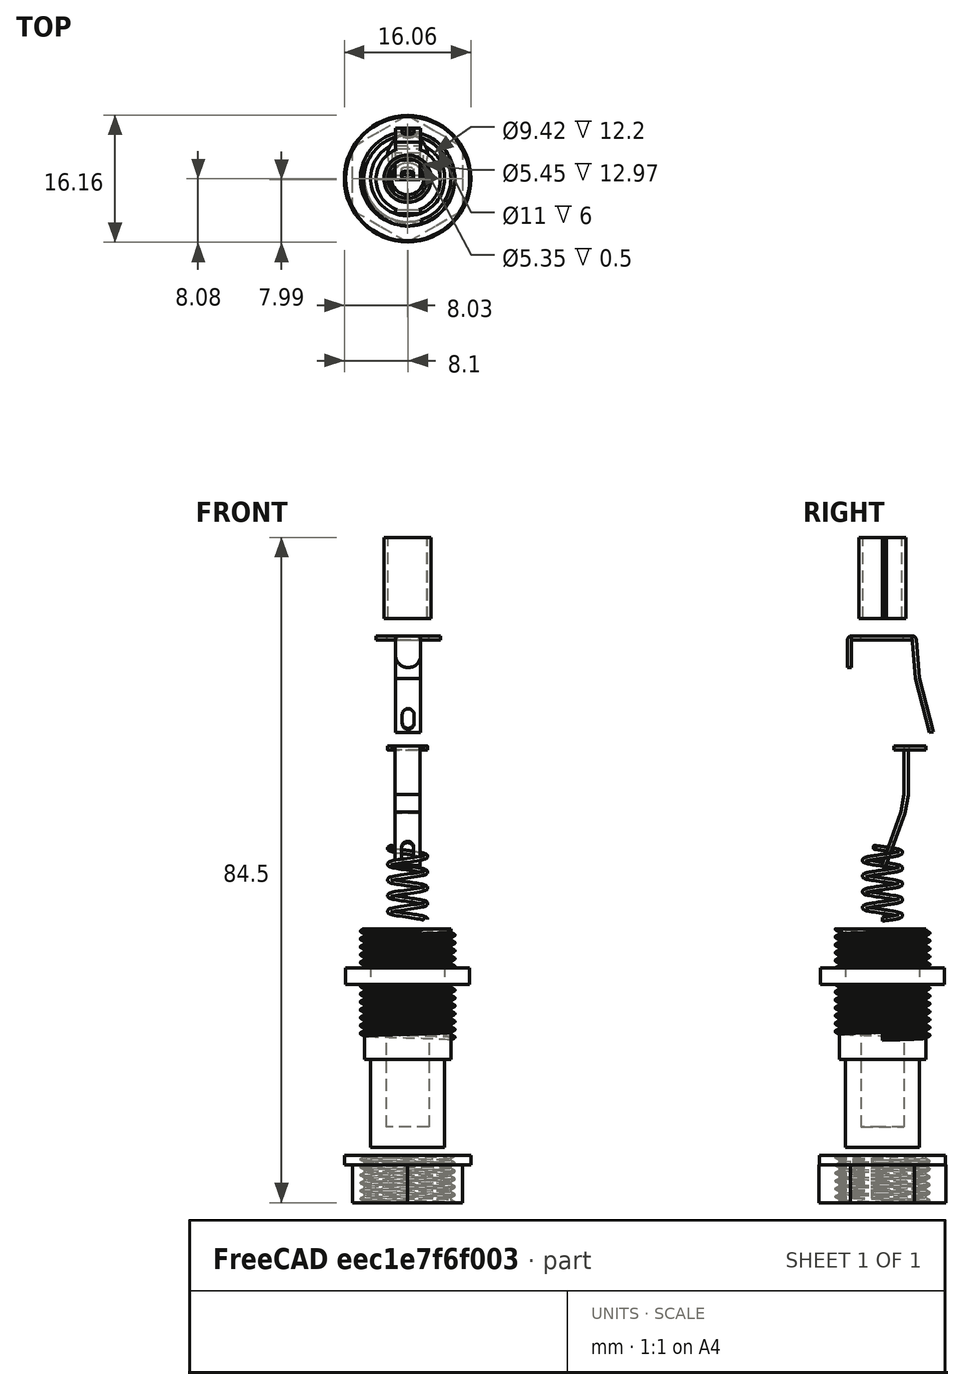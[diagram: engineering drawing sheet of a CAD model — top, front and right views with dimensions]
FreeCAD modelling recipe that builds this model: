
FCSTD DOCUMENT  (FreeCAD 0.15R4671 (Git))
Label: PF15_partlist
License: All rights reserved
LicenseURL: http://en.wikipedia.org/wiki/All_rights_reserved
objects: Part::Part2DObjectPython×15, App::Annotation×8, Part::Feature×7, App::DocumentObjectGroup×2
note: 22 computed .brp shape members not serialized (recipe doc carries the construction recipe); baked Part::Feature solids carry a one-line shape summary decoded from their .brp

FEATURE [Part::Feature] Cut  label="Body"
  Placement = pos=(0,0,-29) rot=(0,0,1;0rad)
  shape: bbox 17.53 x 17.56 x 28.22 mm, 68 faces (baked)
FEATURE [Part::Feature] Sweep  label="Dock"
  Placement = pos=(0,0,-14) rot=(0,0,1;0rad)
  shape: bbox 6.655 x 7.461 x 10.1 mm, 7 faces (baked)
FEATURE [Part::Feature] Cut001  label="plug"
  Placement = pos=(0,0,42) rot=(0,0,1;0rad)
  shape: bbox 17.7 x 17.56 x 14.85 mm, 121 faces (baked)
FEATURE [Part::Feature] Fillet  label="sprat"
  Placement = pos=(0,3,8) rot=(0,1,0;3.14159rad)
  shape: bbox 5.08 x 5.656 x 15.32 mm, 22 faces (baked)
FEATURE [Part::Feature] Cut002  label="HBS_tuerca"
  Placement = pos=(0,0,-47) rot=(1,0,0;3.14159rad)
  shape: bbox 17.68 x 17.56 x 6.935 mm, 42 faces (baked)
FEATURE [Part::Feature] Revolution  label="cap cap"
  Placement = pos=(0,0,31) rot=(1,0,0;1.5708rad)
  shape: bbox 6 x 6 x 10.3 mm, 6 faces (baked)
FEATURE [Part::Feature] Fillet001  label="sprat_ring"
  Placement = pos=(0.07,4,22) rot=(0.707107,0.707107,0;3.14159rad)
  shape: bbox 8.18 x 10.87 x 12.29 mm, 25 faces (baked)
FEATURE [App::Annotation] Text
  LabelText = PF15 | PARTLIST
  Position = (-48,0,42.92)
FEATURE [App::Annotation] Text001
  LabelText = PLUG
  Position = (21.46,0,45)
FEATURE [App::Annotation] Text002
  LabelText = CAP CAP
  Position = (21.46,0,26)
FEATURE [App::Annotation] Text003
  LabelText = SPRAT
  Position = (21.46,0,15)
FEATURE [App::Annotation] Text004
  LabelText = SPRAT RING
  Position = (21.46,0,5)
FEATURE [App::Annotation] Text005
  LabelText = DOCK
  Position = (21.46,0,-5)
FEATURE [App::Annotation] Text006
  LabelText = BODY
  Position = (21.46,0,-30)
FEATURE [App::Annotation] Text007
  LabelText = HBS NUT
  Position = (21.46,0,-45)
FEATURE [Part::Part2DObjectPython] Line  # Draft 2D object (typed FeaturePython)
  ChamferSize = 0
  Closed = false
  End = (19.535,0,43.819)
  FilletRadius = 0
  Length = 10.5027
  MakeFace = true
  Points = (2) [(30.0376,0,43.819),(19.535,0,43.819)]
  Start = (30.0376,0,43.819)
FEATURE [Part::Part2DObjectPython] Line001  # Draft 2D object (typed FeaturePython)
  ChamferSize = 0
  Closed = false
  End = (3.05,0,41.505)
  FilletRadius = 0
  Length = 16.6466
  MakeFace = true
  Points = (2) [(19.535,0,43.819),(3.05,-3.29736e-16,41.505)]
  Start = (19.535,0,43.819)
FEATURE [Part::Part2DObjectPython] Line002  # Draft 2D object (typed FeaturePython)
  ChamferSize = 0
  Closed = false
  End = (19.9494,0,24.9117)
  FilletRadius = 0
  Length = 15.306
  MakeFace = true
  Points = (2) [(35.2553,0,24.9117),(19.9494,0,24.9117)]
  Start = (35.2553,0,24.9117)
FEATURE [Part::Part2DObjectPython] Line003  # Draft 2D object (typed FeaturePython)
  ChamferSize = 0
  Closed = false
  End = (3,0,29.35)
  FilletRadius = 0
  Length = 17.5208
  MakeFace = true
  Points = (2) [(19.9494,0,24.9117),(3,-1.09912e-15,29.35)]
  Start = (19.9494,0,24.9117)
FEATURE [Part::Part2DObjectPython] Line004  # Draft 2D object (typed FeaturePython)
  ChamferSize = 0
  Closed = false
  End = (20.1213,0,14.0771)
  FilletRadius = 0
  Length = 11.1785
  MakeFace = true
  Points = (2) [(31.2999,0,14.0771),(20.1213,0,14.0771)]
  Start = (31.2999,0,14.0771)
FEATURE [Part::Part2DObjectPython] Line005  # Draft 2D object (typed FeaturePython)
  ChamferSize = 0
  Closed = false
  End = (1.66,4.17978,16.5555)
  FilletRadius = 0
  Length = 19.0901
  MakeFace = true
  Points = (2) [(20.1213,0,14.0771),(1.66,4.17978,16.5555)]
  Start = (20.1213,0,14.0771)
FEATURE [Part::Part2DObjectPython] Line006  # Draft 2D object (typed FeaturePython)
  ChamferSize = 0
  Closed = false
  End = (20.1213,0,3.75845)
  FilletRadius = 0
  Length = 20.2933
  MakeFace = true
  Points = (2) [(40.4146,0,3.75845),(20.1213,0,3.75845)]
  Start = (40.4146,0,3.75845)
FEATURE [Part::Part2DObjectPython] Line007  # Draft 2D object (typed FeaturePython)
  ChamferSize = 0
  Closed = false
  End = (1.58,2.53441,0.714356)
  FilletRadius = 0
  Length = 18.9597
  MakeFace = true
  Points = (2) [(20.1213,0,3.75845),(1.58,2.53441,0.714356)]
  Start = (20.1213,0,3.75845)
FEATURE [Part::Part2DObjectPython] Line008  # Draft 2D object (typed FeaturePython)
  ChamferSize = 0
  Closed = false
  End = (20.2933,0,-6.04425)
  FilletRadius = 0
  Length = 9.8027
  MakeFace = true
  Points = (2) [(30.096,0,-6.04425),(20.2933,0,-6.04425)]
  Start = (30.096,0,-6.04425)
FEATURE [Part::Part2DObjectPython] Line009  # Draft 2D object (typed FeaturePython)
  ChamferSize = 0
  Closed = false
  End = (2.55,-6.77986e-07,-10)
  FilletRadius = 0
  Length = 18.1789
  MakeFace = true
  Points = (2) [(20.2933,0,-6.04425),(2.55,-6.77986e-07,-10)]
  Start = (20.2933,0,-6.04425)
FEATURE [Part::Part2DObjectPython] Line010  # Draft 2D object (typed FeaturePython)
  ChamferSize = 0
  Closed = false
  End = (19.9494,0,-31.4969)
  FilletRadius = 0
  Length = 10.1467
  MakeFace = true
  Points = (2) [(30.096,0,-31.4969),(19.9494,0,-31.4969)]
  Start = (30.096,0,-31.4969)
FEATURE [Part::Part2DObjectPython] Line011  # Draft 2D object (typed FeaturePython)
  ChamferSize = 0
  Closed = false
  End = (5.5,0,-29.3637)
  FilletRadius = 0
  Length = 14.606
  MakeFace = true
  Points = (2) [(19.9494,0,-31.4969),(5.5,-4.14142e-15,-29.3637)]
  Start = (19.9494,0,-31.4969)
FEATURE [Part::Part2DObjectPython] Line012  # Draft 2D object (typed FeaturePython)
  ChamferSize = 0
  Closed = false
  End = (19.9551,0,-46.2939)
  FilletRadius = 0
  Length = 14.9138
  MakeFace = true
  Points = (2) [(34.8689,0,-46.2939),(19.9551,0,-46.2939)]
  Start = (34.8689,0,-46.2939)
FEATURE [Part::Part2DObjectPython] Line013  # Draft 2D object (typed FeaturePython)
  ChamferSize = 0
  Closed = false
  End = (7,-4.04145,-47.6)
  FilletRadius = 0
  Length = 13.6335
  MakeFace = true
  Points = (2) [(19.9551,0,-46.2939),(7,-4.04145,-47.6)]
  Start = (19.9551,0,-46.2939)
FEATURE [App::DocumentObjectGroup] Group  label="Lines"
  Group = -> [Line013,Line012,Line011,Line010,Line008,Line007,Line006,Line005,Line004,Line003,Line002,Line001,Line,Line009]
FEATURE [App::DocumentObjectGroup] Group001  label="Text008"
  Group = -> [Text,Text001,Text002,Text003,Text004,Text005,Text006,Text007]
FEATURE [Part::Part2DObjectPython] Rectangle  # Draft 2D object (typed FeaturePython)
  ChamferSize = 0
  FilletRadius = 0
  Height = -115.15
  Length = 95.6747
  MakeFace = true
  Placement = pos=(-54.4296,0,58.7819) rot=(1,0,0;1.5708rad)
